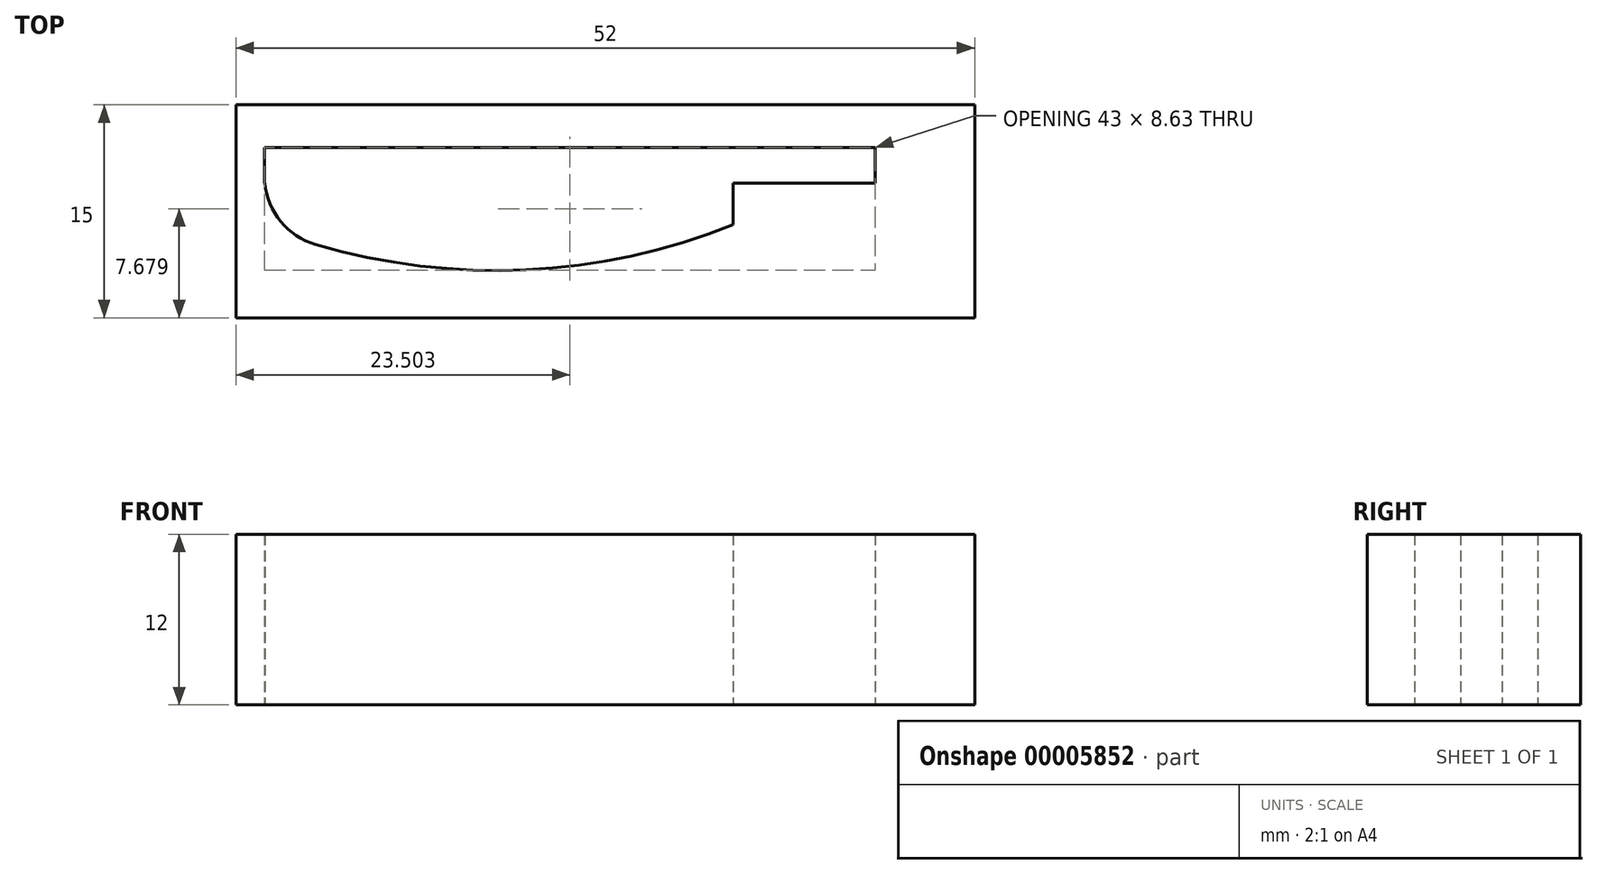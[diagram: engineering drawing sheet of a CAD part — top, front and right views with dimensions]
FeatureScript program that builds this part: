
annotation { "Feature Type Name" : "Feature", "Feature Type Description" : "" }
export const myFeature = defineFeature(function(context is Context, id is Id, definition is map)
    precondition{}
    {
        {
            var Q0;
            Q0=qCreatedBy(makeId("Top.planeOp"),FACE);
            var sketch = newSketch(context, id + "F0", { "sketchPlane" : qUnion([Q0])});
            skLineSegment(sketch, "E0.bottom", {"start": v(-37.08, 3.69) * mm, "end": v(12.92, 3.69) * mm});
            skLineSegment(sketch, "E0.top", {"start": v(-37.08, -11.31) * mm, "end": v(12.92, -11.31) * mm});
            skLineSegment(sketch, "E0.left", {"start": v(-37.08, 3.69) * mm, "end": v(-37.08, -1.35) * mm});
            skLineSegment(sketch, "E0.right", {"start": v(12.92, 3.69) * mm, "end": v(12.92, -11.31) * mm});
            skLineSegment(sketch, "E1.bottom", {"start": v(-37.08, 0.69) * mm, "end": v(5.92, 0.69) * mm});
            skLineSegment(sketch, "E1.top", {"start": v(-37.08, -1.81) * mm, "end": v(5.92, -1.81) * mm});
            skLineSegment(sketch, "E1.left", {"start": v(-37.08, 0.69) * mm, "end": v(-37.08, -1.81) * mm});
            skLineSegment(sketch, "E1.right", {"start": v(5.92, 0.69) * mm, "end": v(5.92, -1.81) * mm});
            skLineSegment(sketch, "E2", {"start": v(-4.08, -1.81) * mm, "end": v(-4.08, -11.31) * mm});
            skArc(sketch, "E3", {"start": v(-33.49, -6.15) * mm, "mid": v(-18.66, -7.93) * mm, "end": v(-4.08, -4.76) * mm});
            skPoint(sketch, "E4.newPointA", {"position": v(-37.5, -4.76) * mm});
            skArc(sketch, "E4.filletArc", {"start": v(-37.08, -1.35) * mm, "mid": v(-36.08, -4.35) * mm, "end": v(-33.49, -6.15) * mm});
            skLineSegment(sketch, "E5", {"start": v(-37.08, -11.31) * mm, "end": v(-37.08, -1.81) * mm});
            skLineSegment(sketch, "E6", {"start": v(-37.08, -11.31) * mm, "end": v(-39.08, -11.31) * mm});
            skLineSegment(sketch, "E7", {"start": v(-39.08, -11.31) * mm, "end": v(-39.08, 3.69) * mm});
            skLineSegment(sketch, "E8", {"start": v(-39.08, 3.69) * mm, "end": v(-37.08, 3.69) * mm});
            skSolve(sketch);
        }
        {
            var Q0;
            Q0 = qSketchRegion(id + "F0", true);
            extrude(context, id + "F1", {"entities" : qUnion([Q0]), "depth" : 12 * mm});
        }
    });
